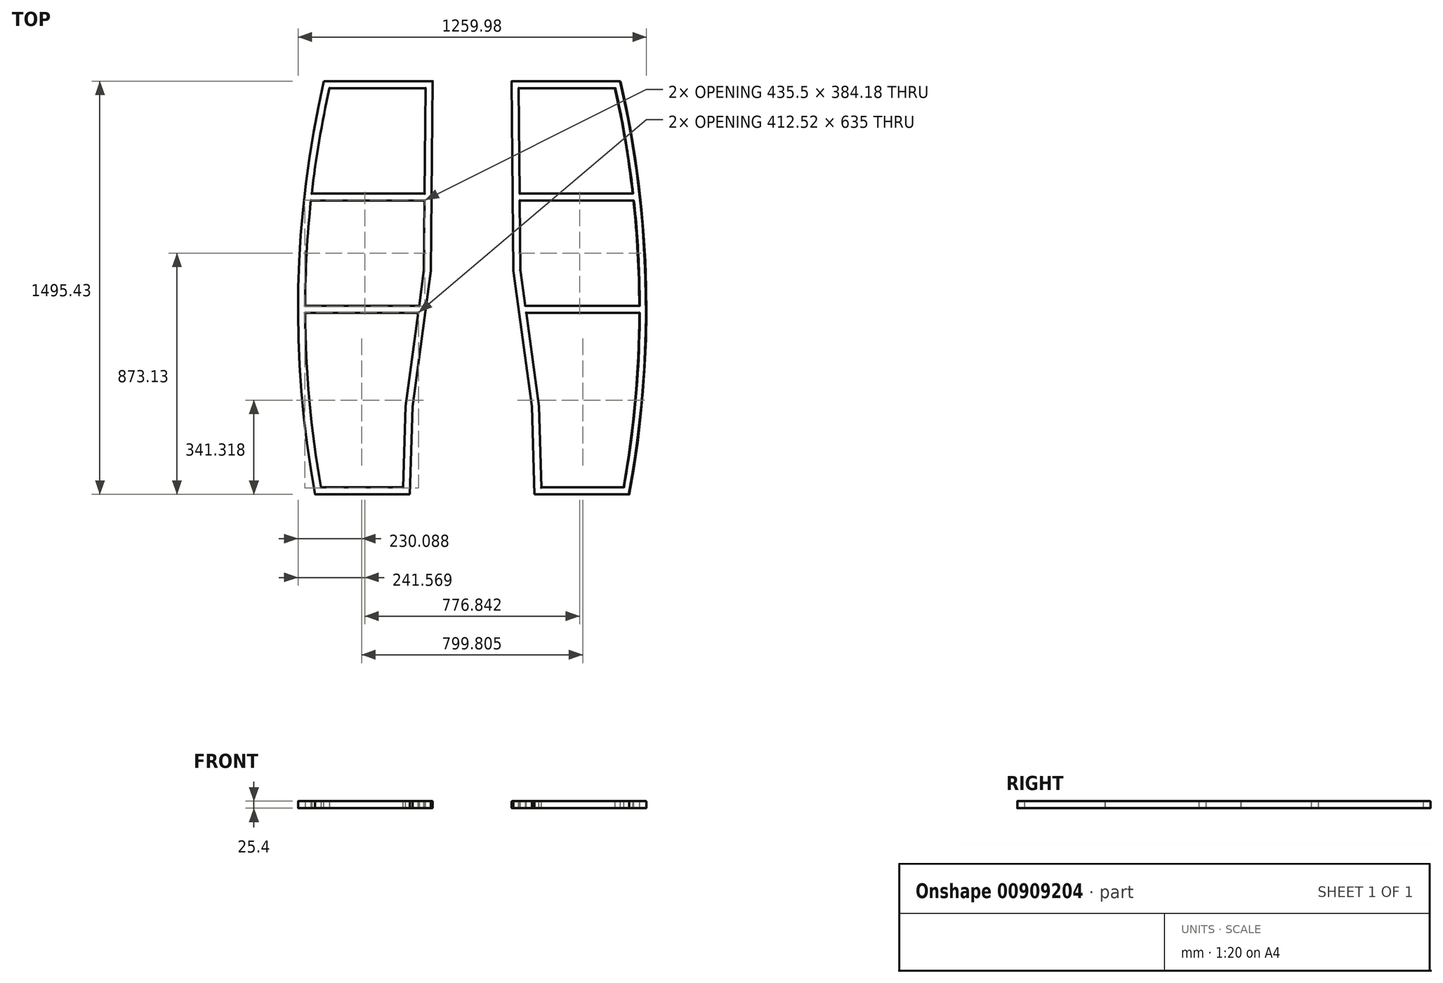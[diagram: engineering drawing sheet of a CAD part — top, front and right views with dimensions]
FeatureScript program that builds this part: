
annotation { "Feature Type Name" : "Feature", "Feature Type Description" : "" }
export const myFeature = defineFeature(function(context is Context, id is Id, definition is map)
    precondition{}
    {
        {
            var Q0;
            Q0=qCreatedBy(makeId("Front.planeOp"),FACE);
            var sketch = newSketch(context, id + "F0", { "sketchPlane" : qUnion([Q0])});
            skLineSegment(sketch, "E0", {"start": v(0, 0) * mm, "end": v(0, -387.35) * mm, "construction": true});
            skLineSegment(sketch, "E1", {"start": v(0, -387.35) * mm, "end": v(0, -679.45) * mm, "construction": true});
            skLineSegment(sketch, "E2", {"start": v(0, -679.45) * mm, "end": v(-142.87, -679.45) * mm, "construction": true});
            skLineSegment(sketch, "E3", {"start": v(-142.87, -679.45) * mm, "end": v(-536.57, -679.45) * mm, "construction": true});
            skSolve(sketch);
        }
        {
            var Q0;
            Q0=sQuery(id+"F0.wireOp",EDGE,"E1");
            var Q1;
            Q1=sQuery(id+"F0.wireOp",VERTEX,"E1.end");
            cPlane(context, id + "F1", {"entities" : qUnion([Q0, Q1]), "cplaneType" : CPlaneType.LINE_POINT, "offset" : 25.4 * mm, "width" : 152.4 * mm, "height" : 152.4 * mm});
        }
        {
            var Q0;
            Q0=qCreatedBy(id+"F1.planeOp",FACE);
            var sketch = newSketch(context, id + "F2", { "sketchPlane" : qUnion([Q0])});
            skLineSegment(sketch, "E4", {"start": v(0, 0) * mm, "end": v(-142.88, 0) * mm, "construction": true});
            skLineSegment(sketch, "E5", {"start": v(-142.88, 0) * mm, "end": v(-142.88, 12.7) * mm, "construction": true});
            skLineSegment(sketch, "E6", {"start": v(-142.88, 12.7) * mm, "end": v(-536.58, 12.7) * mm, "construction": true});
            skLineSegment(sketch, "E7", {"start": v(-536.58, 12.7) * mm, "end": v(-536.58, 0) * mm, "construction": true});
            skLineSegment(sketch, "E8", {"start": v(-536.58, 0) * mm, "end": v(-142.88, 0) * mm, "construction": true});
            skLineSegment(sketch, "E9", {"start": v(-142.88, 0) * mm, "end": v(-142.88, 673.1) * mm, "construction": true});
            skLineSegment(sketch, "E10", {"start": v(-142.88, 673.1) * mm, "end": v(-149.23, 673.1) * mm, "construction": true});
            skLineSegment(sketch, "E11", {"start": v(-536.58, 0) * mm, "end": v(-536.58, -12.7) * mm, "construction": true});
            skLineSegment(sketch, "E12", {"start": v(-536.58, -12.7) * mm, "end": v(-142.88, -12.7) * mm, "construction": true});
            skLineSegment(sketch, "E13", {"start": v(-142.88, -12.7) * mm, "end": v(-142.88, 0) * mm, "construction": true});
            skLineSegment(sketch, "E14", {"start": v(-142.87, -12.7) * mm, "end": v(-149.23, 673.1) * mm});
            skLineSegment(sketch, "E15", {"start": v(-149.23, 673.1) * mm, "end": v(-174.62, 672.86) * mm});
            skLineSegment(sketch, "E16", {"start": v(-174.62, 672.86) * mm, "end": v(-168.51, 12.7) * mm});
            skLineSegment(sketch, "E17", {"start": v(-339.73, 0) * mm, "end": v(-339.73, 406.4) * mm, "construction": true});
            skLineSegment(sketch, "E18", {"start": v(-161.92, 672.98) * mm, "end": v(-155.7, 0) * mm});
            skLineSegment(sketch, "E19", {"start": v(-339.73, 406.4) * mm, "end": v(-172.16, 406.4) * mm});
            skLineSegment(sketch, "E20", {"start": v(-172.16, 406.4) * mm, "end": v(-159.46, 406.52) * mm});
            skLineSegment(sketch, "E21", {"start": v(-339.73, 406.4) * mm, "end": v(-339.73, 419.1) * mm});
            skLineSegment(sketch, "E22", {"start": v(-339.73, 406.4) * mm, "end": v(-339.73, 393.7) * mm});
            skLineSegment(sketch, "E23", {"start": v(-339.73, 393.7) * mm, "end": v(-172.04, 393.7) * mm});
            skLineSegment(sketch, "E24", {"start": v(-339.73, 419.1) * mm, "end": v(-172.27, 419.1) * mm});
            skLineSegment(sketch, "E25", {"start": v(-172.27, 419.1) * mm, "end": v(-585.02, 419.1) * mm});
            skLineSegment(sketch, "E26", {"start": v(0, 0) * mm, "end": v(0.12, -12.7) * mm, "construction": true});
            skLineSegment(sketch, "E27", {"start": v(0.12, -12.7) * mm, "end": v(0.12, 1482.73) * mm, "construction": true});
            skLineSegment(sketch, "E28", {"start": v(0.12, 1482.73) * mm, "end": v(-225.3, 1482.73) * mm, "construction": true});
            skLineSegment(sketch, "E29", {"start": v(-225.3, 1482.73) * mm, "end": v(-568.2, 1482.73) * mm, "construction": true});
            skLineSegment(sketch, "E30", {"start": v(-339.73, 406.4) * mm, "end": v(-339.73, 812.8) * mm, "construction": true});
            skLineSegment(sketch, "E31.bottom", {"start": v(-568.2, 1482.73) * mm, "end": v(-225.3, 1482.73) * mm});
            skLineSegment(sketch, "E31.top", {"start": v(-568.2, 1457.33) * mm, "end": v(-225.3, 1457.33) * mm});
            skLineSegment(sketch, "E31.left", {"start": v(-568.2, 1482.73) * mm, "end": v(-568.2, 1457.33) * mm});
            skLineSegment(sketch, "E32", {"start": v(-215.78, 1165.37) * mm, "end": v(-225.3, 1482.73) * mm});
            skLineSegment(sketch, "E33", {"start": v(-215.78, 1165.37) * mm, "end": v(0.12, 1165.37) * mm, "construction": true});
            skLineSegment(sketch, "E34", {"start": v(-225.3, 1482.73) * mm, "end": v(-225.3, 1457.33) * mm});
            skLineSegment(sketch, "E35", {"start": v(-215.78, 1165.37) * mm, "end": v(-149.23, 673.1) * mm});
            skLineSegment(sketch, "E36", {"start": v(-174.62, 672.86) * mm, "end": v(-241.19, 1165.19) * mm});
            skLineSegment(sketch, "E37", {"start": v(-220.54, 1324.05) * mm, "end": v(-245.93, 1323.28) * mm});
            skLineSegment(sketch, "E38", {"start": v(-245.93, 1323.28) * mm, "end": v(-241.19, 1165.19) * mm});
            skLineSegment(sketch, "E39", {"start": v(-215.78, 1165.37) * mm, "end": v(-241.19, 1165.19) * mm});
            skLineSegment(sketch, "E40", {"start": v(-245.93, 1323.28) * mm, "end": v(-250.72, 1482.73) * mm});
            skLineSegment(sketch, "E41", {"start": v(-339.73, 812.8) * mm, "end": v(-193.54, 812.8) * mm});
            skLineSegment(sketch, "E42", {"start": v(-339.73, 812.8) * mm, "end": v(-617.3, 812.8) * mm});
            skLineSegment(sketch, "E43", {"start": v(-339.73, 393.7) * mm, "end": v(-606.23, 393.7) * mm});
            skLineSegment(sketch, "E44", {"start": v(-339.73, 812.8) * mm, "end": v(-339.73, 800.1) * mm});
            skLineSegment(sketch, "E45", {"start": v(-339.73, 800.1) * mm, "end": v(-191.83, 800.1) * mm});
            skLineSegment(sketch, "E46", {"start": v(-191.83, 800.1) * mm, "end": v(-604.58, 800.1) * mm});
            skLineSegment(sketch, "E47", {"start": v(-339.73, 812.8) * mm, "end": v(-339.73, 825.5) * mm});
            skLineSegment(sketch, "E48", {"start": v(-339.73, 825.5) * mm, "end": v(-195.26, 825.5) * mm});
            skLineSegment(sketch, "E49", {"start": v(-339.73, 825.5) * mm, "end": v(-629.97, 825.5) * mm});
            skLineSegment(sketch, "E50", {"start": v(-339.73, 406.4) * mm, "end": v(-594.88, 406.4) * mm});
            skLineSegment(sketch, "E51", {"start": v(-604.58, 800.1) * mm, "end": v(-629.98, 800.1) * mm});
            skLineSegment(sketch, "E52", {"start": v(-585.02, 419.1) * mm, "end": v(-609.04, 419.1) * mm});
            skArc(sketch, "E53", {"start": v(-568.2, 1482.73) * mm, "mid": v(-629.17, 733.39) * mm, "end": v(-536.58, -12.7) * mm});
            skArc(sketch, "E54.0", {"start": v(-544.72, 1470.03) * mm, "mid": v(-603.77, 733.42) * mm, "end": v(-513.42, 0) * mm});
            skArc(sketch, "E55.0", {"start": v(-555.29, 1482.73) * mm, "mid": v(-616.6, 739.89) * mm, "end": v(-526.45, 0) * mm});
            skLineSegment(sketch, "E56", {"start": v(-568.2, 1470.03) * mm, "end": v(-225.3, 1470.03) * mm});
            skLineSegment(sketch, "E57", {"start": v(-233.24, 1323.67) * mm, "end": v(-238.01, 1482.73) * mm});
            skLineSegment(sketch, "E58", {"start": v(-233.24, 1323.67) * mm, "end": v(-228.49, 1165.28) * mm});
            skLineSegment(sketch, "E59", {"start": v(-536.58, 0) * mm, "end": v(-142.88, 0) * mm});
            skLineSegment(sketch, "E60", {"start": v(-536.58, -12.7) * mm, "end": v(-142.88, -12.7) * mm});
            skLineSegment(sketch, "E61", {"start": v(-193.54, 812.8) * mm, "end": v(-180.84, 812.8) * mm});
            skSolve(sketch);
        }
        {
            var Q0;
            Q0=sQuery(id+"F0.wireOp",EDGE,"E3");
            var Q1;
            Q1=sQuery(id+"F0.wireOp",VERTEX,"E3.end");
            cPlane(context, id + "F3", {"entities" : qUnion([Q0, Q1]), "cplaneType" : CPlaneType.LINE_POINT, "offset" : 25.4 * mm, "width" : 152.4 * mm, "height" : 152.4 * mm});
        }
        {
            var Q0;
            Q0=qCreatedBy(id+"F3.planeOp",FACE);
            var sketch = newSketch(context, id + "F4", { "sketchPlane" : qUnion([Q0])});
            skLineSegment(sketch, "E62.bottom", {"start": v(-11.11, -679.45) * mm, "end": v(11.11, -679.45) * mm});
            skLineSegment(sketch, "E62.top", {"start": v(-11.11, -654.05) * mm, "end": v(11.11, -654.05) * mm});
            skLineSegment(sketch, "E62.left", {"start": v(-12.7, -677.86) * mm, "end": v(-12.7, -655.64) * mm});
            skLineSegment(sketch, "E62.right", {"start": v(12.7, -677.86) * mm, "end": v(12.7, -655.64) * mm});
            skPoint(sketch, "E62.middle", {"position": v(0, -666.75) * mm});
            skPoint(sketch, "E63.visualSharp", {"position": v(12.7, -654.05) * mm});
            skArc(sketch, "E63.filletArc", {"start": v(12.7, -655.64) * mm, "mid": v(12.24, -654.51) * mm, "end": v(11.11, -654.05) * mm});
            skPoint(sketch, "E64.visualSharp", {"position": v(-12.7, -654.05) * mm});
            skArc(sketch, "E64.filletArc", {"start": v(-11.11, -654.05) * mm, "mid": v(-12.24, -654.51) * mm, "end": v(-12.7, -655.64) * mm});
            skPoint(sketch, "E65.visualSharp", {"position": v(-12.7, -679.45) * mm});
            skArc(sketch, "E65.filletArc", {"start": v(-12.7, -677.86) * mm, "mid": v(-12.24, -678.99) * mm, "end": v(-11.11, -679.45) * mm});
            skPoint(sketch, "E66.visualSharp", {"position": v(12.7, -679.45) * mm});
            skArc(sketch, "E66.filletArc", {"start": v(11.11, -679.45) * mm, "mid": v(12.24, -678.99) * mm, "end": v(12.7, -677.86) * mm});
            skPoint(sketch, "E67.end.orphan", {"position": v(0, -679.45) * mm});
            skSolve(sketch);
        }
        {
            var Q0;
            Q0=makeQuery(id+"F4.imprint","IMPRINT",FACE,{"disambiguationData":[TD([[makeQuery(id+"F4.imprint","IMPRINT",EDGE,{"derivedFrom":sQuery(id+"F4.wireOp",EDGE,"E62.bottom")}),1.0]])]});
            var Q1;
            Q1=sQuery(id+"F2.wireOp",EDGE,"E60");
            var Q2;
            Q2=sQuery(id+"F2.wireOp",EDGE,"E14");
            var Q3;
            Q3=sQuery(id+"F2.wireOp",EDGE,"E35");
            var Q4;
            Q4=sQuery(id+"F2.wireOp",EDGE,"E32");
            var Q5;
            Q5=sQuery(id+"F2.wireOp",EDGE,"E31.bottom");
            var Q6;
            Q6=sQuery(id+"F2.wireOp",EDGE,"E53");
            sweep(context, id + "F5", {"profiles" : qUnion([Q0]), "path" : qUnion([Q1, Q2, Q3, Q4, Q5, Q6])});
        }
        {
            var Q0;
            Q0=sQuery(id+"F2.wireOp",EDGE,"E19");
            var Q1;
            Q1=sQuery(id+"F2.wireOp",VERTEX,"E17.end");
            cPlane(context, id + "F6", {"entities" : qUnion([Q0, Q1]), "cplaneType" : CPlaneType.LINE_POINT, "offset" : 25.4 * mm, "width" : 152.4 * mm, "height" : 152.4 * mm});
        }
        {
            var Q0;
            Q0=qCreatedBy(id+"F6.planeOp",FACE);
            var sketch = newSketch(context, id + "F7", { "sketchPlane" : qUnion([Q0])});
            skLineSegment(sketch, "E68.bottom", {"start": v(-395.29, -679.45) * mm, "end": v(-417.51, -679.45) * mm});
            skLineSegment(sketch, "E68.top", {"start": v(-395.29, -654.05) * mm, "end": v(-417.51, -654.05) * mm});
            skLineSegment(sketch, "E68.left", {"start": v(-393.7, -677.86) * mm, "end": v(-393.7, -655.64) * mm});
            skLineSegment(sketch, "E68.right", {"start": v(-419.1, -677.86) * mm, "end": v(-419.1, -655.64) * mm});
            skPoint(sketch, "E68.middle", {"position": v(-406.4, -666.75) * mm});
            skPoint(sketch, "E69.visualSharp", {"position": v(-419.1, -654.05) * mm});
            skArc(sketch, "E69.filletArc", {"start": v(-417.51, -654.05) * mm, "mid": v(-418.64, -654.51) * mm, "end": v(-419.1, -655.64) * mm});
            skPoint(sketch, "E70.visualSharp", {"position": v(-393.7, -654.05) * mm});
            skArc(sketch, "E70.filletArc", {"start": v(-393.7, -655.64) * mm, "mid": v(-394.16, -654.51) * mm, "end": v(-395.29, -654.05) * mm});
            skPoint(sketch, "E71.visualSharp", {"position": v(-393.7, -679.45) * mm});
            skArc(sketch, "E71.filletArc", {"start": v(-395.29, -679.45) * mm, "mid": v(-394.16, -678.99) * mm, "end": v(-393.7, -677.86) * mm});
            skPoint(sketch, "E72.visualSharp", {"position": v(-419.1, -679.45) * mm});
            skArc(sketch, "E72.filletArc", {"start": v(-419.1, -677.86) * mm, "mid": v(-418.64, -678.99) * mm, "end": v(-417.51, -679.45) * mm});
            skLineSegment(sketch, "E73", {"start": v(-406.4, -666.75) * mm, "end": v(-406.4, -679.45) * mm});
            skLineSegment(sketch, "E74.bottom", {"start": v(-801.69, -679.45) * mm, "end": v(-823.91, -679.45) * mm});
            skLineSegment(sketch, "E74.top", {"start": v(-801.69, -654.05) * mm, "end": v(-823.91, -654.05) * mm});
            skLineSegment(sketch, "E74.left", {"start": v(-800.1, -677.86) * mm, "end": v(-800.1, -655.64) * mm});
            skLineSegment(sketch, "E74.right", {"start": v(-825.5, -677.86) * mm, "end": v(-825.5, -655.64) * mm});
            skPoint(sketch, "E74.middle", {"position": v(-812.8, -666.75) * mm});
            skLineSegment(sketch, "E75", {"start": v(-812.8, -666.75) * mm, "end": v(-812.8, -679.45) * mm});
            skPoint(sketch, "E76.visualSharp", {"position": v(-825.5, -654.05) * mm});
            skArc(sketch, "E76.filletArc", {"start": v(-823.91, -654.05) * mm, "mid": v(-825.04, -654.51) * mm, "end": v(-825.5, -655.64) * mm});
            skPoint(sketch, "E77.visualSharp", {"position": v(-800.1, -654.05) * mm});
            skArc(sketch, "E77.filletArc", {"start": v(-800.1, -655.64) * mm, "mid": v(-800.56, -654.51) * mm, "end": v(-801.69, -654.05) * mm});
            skPoint(sketch, "E78.visualSharp", {"position": v(-800.1, -679.45) * mm});
            skArc(sketch, "E78.filletArc", {"start": v(-801.69, -679.45) * mm, "mid": v(-800.56, -678.99) * mm, "end": v(-800.1, -677.86) * mm});
            skPoint(sketch, "E79.visualSharp", {"position": v(-825.5, -679.45) * mm});
            skArc(sketch, "E79.filletArc", {"start": v(-825.5, -677.86) * mm, "mid": v(-825.04, -678.99) * mm, "end": v(-823.91, -679.45) * mm});
            skSolve(sketch);
        }
        {
            var Q0;
            Q0=makeQuery(id+"F7.imprint","IMPRINT",FACE,{"disambiguationData":[TD([[makeQuery(id+"F7.imprint","IMPRINT",EDGE,{"derivedFrom":sQuery(id+"F7.wireOp",EDGE,"E68.top")}),1.0]])]});
            var Q1;
            Q1=sQuery(id+"F2.wireOp",EDGE,"E19");
            var Q2;
            Q2=sQuery(id+"F2.wireOp",EDGE,"E20");
            var Q3;
            Q3=sQuery(id+"F2.wireOp",EDGE,"E50");
            sweep(context, id + "F8", {"operationType" : NewBodyOperationType.ADD, "profiles" : qUnion([Q0]), "path" : qUnion([Q1, Q2, Q3])});
        }
        {
            var Q0;
            Q0=makeQuery(id+"F7.imprint","IMPRINT",FACE,{"disambiguationData":[TD([[makeQuery(id+"F7.imprint","IMPRINT",EDGE,{"derivedFrom":sQuery(id+"F7.wireOp",EDGE,"E74.top")}),1.0]])]});
            var Q1;
            Q1=sQuery(id+"F2.wireOp",EDGE,"E42");
            var Q2;
            Q2=sQuery(id+"F2.wireOp",EDGE,"E41");
            var Q3;
            Q3=sQuery(id+"F2.wireOp",EDGE,"E61");
            sweep(context, id + "F9", {"operationType" : NewBodyOperationType.ADD, "profiles" : qUnion([Q0]), "path" : qUnion([Q1, Q2, Q3])});
        }
        {
            var Q0;
            Q0=makeQuery(id+"F5.opSweep","SWEPT_BODY",BODY,{"disambiguationData":[OSD([sQuery(id+"F2.wireOp",EDGE,"E53"),sQuery(id+"F4.wireOp",EDGE,"E62.bottom"),sQuery(id+"F4.wireOp",EDGE,"E62.top"),sQuery(id+"F4.wireOp",EDGE,"E62.left"),sQuery(id+"F4.wireOp",EDGE,"E62.right"),sQuery(id+"F4.wireOp",EDGE,"E63.filletArc"),sQuery(id+"F4.wireOp",EDGE,"E64.filletArc"),sQuery(id+"F4.wireOp",EDGE,"E65.filletArc"),sQuery(id+"F4.wireOp",EDGE,"E66.filletArc")])]});
            var Q1;
            Q1=qCreatedBy(makeId("Right.planeOp"),FACE);
            mirror(context, id + "F10", {"entities" : qUnion([Q0]), "mirrorPlane" : qUnion([Q1])});
        }
    });
